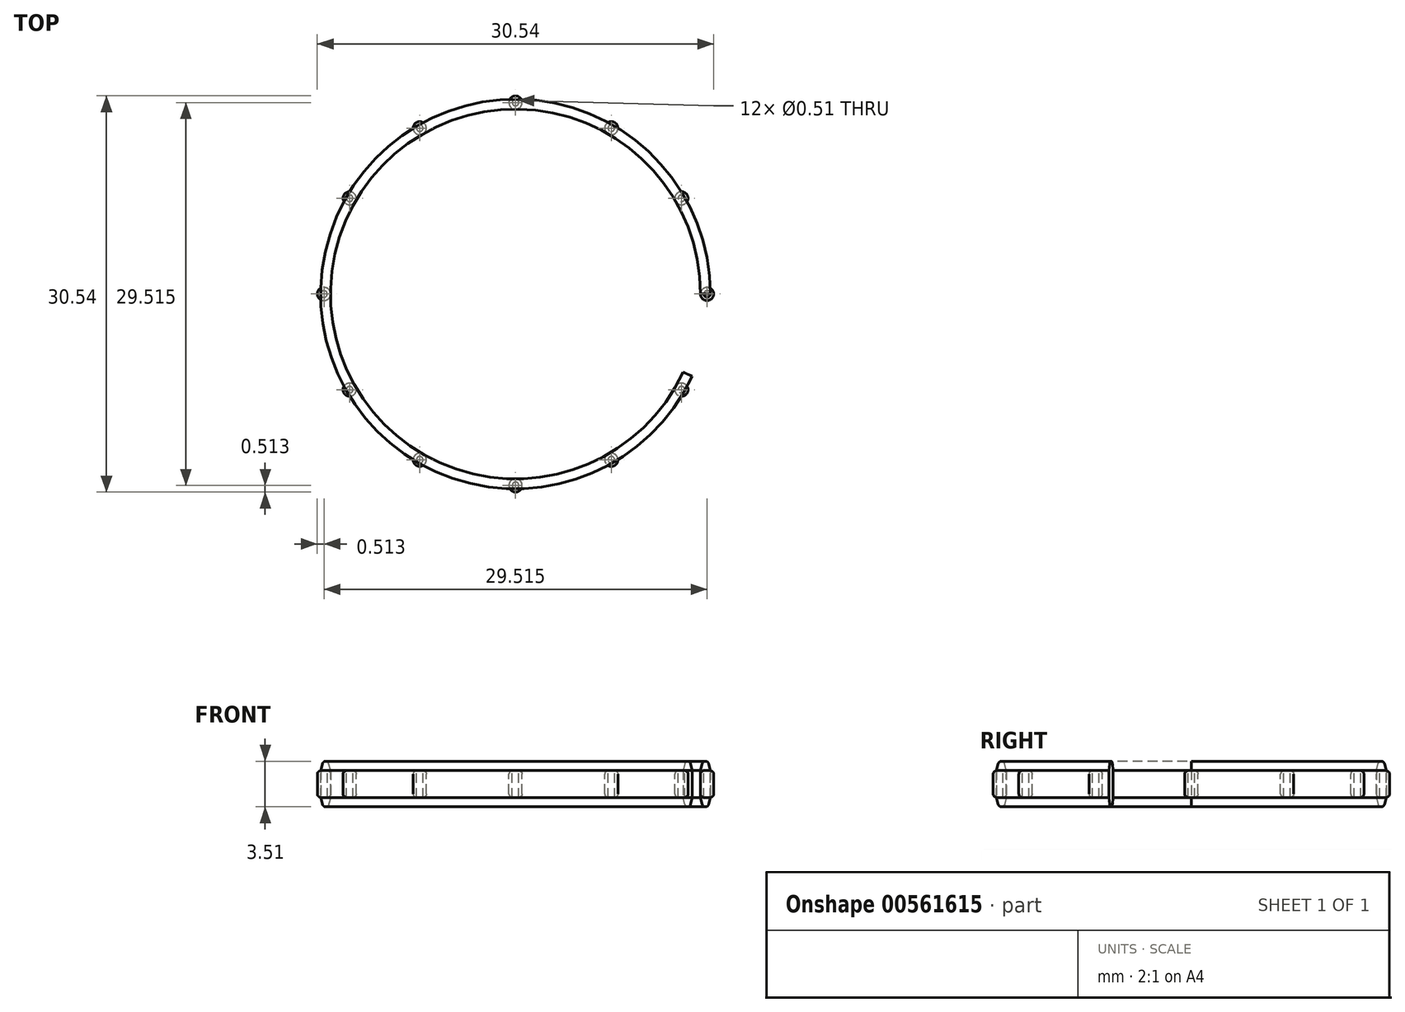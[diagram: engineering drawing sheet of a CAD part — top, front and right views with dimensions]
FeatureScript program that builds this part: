
annotation { "Feature Type Name" : "Feature", "Feature Type Description" : "" }
export const myFeature = defineFeature(function(context is Context, id is Id, definition is map)
    precondition{}
    {
        {
            var Q0;
            Q0=qCreatedBy(makeId("Front.planeOp"),FACE);
            var sketch = newSketch(context, id + "F0", { "sketchPlane" : qUnion([Q0])});
            skLineSegment(sketch, "E0", {"start": v(0, 0) * mm, "end": v(0, 3.94) * mm, "construction": true});
            skLineSegment(sketch, "E1", {"start": v(14.36, 2.54) * mm, "end": v(14.36, 0) * mm, "construction": true});
            skLineSegment(sketch, "E2", {"start": v(14.36, 0) * mm, "end": v(7.64, 0) * mm, "construction": true});
            skLineSegment(sketch, "E3", {"start": v(14.36, 2.54) * mm, "end": v(15.38, 2.54) * mm, "construction": true});
            skLineSegment(sketch, "E4", {"start": v(15.38, 2.54) * mm, "end": v(15.38, 0) * mm, "construction": true});
            skLineSegment(sketch, "E5", {"start": v(15.38, 0) * mm, "end": v(15.5, 0) * mm, "construction": true});
            skLineSegment(sketch, "E6", {"start": v(15.5, 0) * mm, "end": v(16, 0.5) * mm, "construction": true});
            skLineSegment(sketch, "E7", {"start": v(16, 0.5) * mm, "end": v(16, 4.02) * mm, "construction": true});
            skLineSegment(sketch, "E8", {"start": v(15.01, 1.85) * mm, "end": v(14.88, 2.35) * mm});
            skLineSegment(sketch, "E9", {"start": v(14.39, 2.35) * mm, "end": v(14.25, 1.85) * mm});
            skPoint(sketch, "E10.visualSharp", {"position": v(14.63, 3.27) * mm});
            skArc(sketch, "E10.filletArc", {"start": v(14.88, 2.35) * mm, "mid": v(14.63, 2.54) * mm, "end": v(14.39, 2.35) * mm});
            skArc(sketch, "E11.MirrorCS", {"start": v(14.88, -0.78) * mm, "mid": v(14.63, -0.97) * mm, "end": v(14.39, -0.78) * mm});
            skLineSegment(sketch, "E12.MirrorCS", {"start": v(15.01, -0.27) * mm, "end": v(14.88, -0.78) * mm});
            skLineSegment(sketch, "E13", {"start": v(13.69, -0.1) * mm, "end": v(16.72, -0.1) * mm, "construction": true});
            skLineSegment(sketch, "E14", {"start": v(13.24, -0.36) * mm, "end": v(17.66, -0.36) * mm, "construction": true});
            skLineSegment(sketch, "E15", {"start": v(13.22, -0.69) * mm, "end": v(17.76, -0.69) * mm, "construction": true});
            skLineSegment(sketch, "E16", {"start": v(14.63, 2.29) * mm, "end": v(14.63, -0.71) * mm, "construction": true});
            skLineSegment(sketch, "E17.trimOffspring", {"start": v(14.39, -0.78) * mm, "end": v(14.25, -0.27) * mm});
            skLineSegment(sketch, "E18", {"start": v(14.25, 1.85) * mm, "end": v(14.25, -0.27) * mm});
            skLineSegment(sketch, "E19", {"start": v(15.01, 1.85) * mm, "end": v(15.01, -0.27) * mm});
            skLineSegment(sketch, "E20.bottom", {"start": v(17.46, 3.65) * mm, "end": v(18.48, 3.65) * mm});
            skLineSegment(sketch, "E20.top", {"start": v(17.46, 1.01) * mm, "end": v(18.48, 1.01) * mm});
            skLineSegment(sketch, "E20.left", {"start": v(17.46, 3.65) * mm, "end": v(17.46, 1.01) * mm});
            skLineSegment(sketch, "E20.right", {"start": v(18.48, 3.65) * mm, "end": v(18.48, 1.01) * mm});
            skLineSegment(sketch, "E21", {"start": v(15.01, 1.85) * mm, "end": v(15.14, 1.77) * mm});
            skLineSegment(sketch, "E22", {"start": v(15.27, 1.55) * mm, "end": v(15.27, 0.02) * mm});
            skLineSegment(sketch, "E23", {"start": v(15.14, -0.2) * mm, "end": v(15.01, -0.27) * mm});
            skLineSegment(sketch, "E24", {"start": v(14.76, 2) * mm, "end": v(14.76, 0.25) * mm, "construction": true});
            skPoint(sketch, "E25.visualSharp", {"position": v(15.27, 1.7) * mm});
            skArc(sketch, "E25.filletArc", {"start": v(15.27, 1.55) * mm, "mid": v(15.23, 1.68) * mm, "end": v(15.14, 1.77) * mm});
            skPoint(sketch, "E26.visualSharp", {"position": v(15.27, -0.12) * mm});
            skArc(sketch, "E26.filletArc", {"start": v(15.14, -0.2) * mm, "mid": v(15.23, -0.1) * mm, "end": v(15.27, 0.02) * mm});
            skSolve(sketch);
        }
        {
            var Q0;
            Q0=makeQuery(id+"F0.imprint","IMPRINT",FACE,{"disambiguationData":[TD([[makeQuery(id+"F0.imprint","IMPRINT",EDGE,{"derivedFrom":sQuery(id+"F0.wireOp",EDGE,"E19")}),1.0]])]});
            var Q1;
            Q1=sQuery(id+"F0.wireOp",EDGE,"E24");
            revolve(context, id + "F1", {"entities" : qUnion([Q0]), "axis" : qUnion([Q1]), "revolveType" : RevolveType.FULL});
        }
        {
            var Q0;
            Q0=makeQuery(id+"F1.opRevolve","SWEPT_BODY",BODY,{"disambiguationData":[OSD([sQuery(id+"F0.wireOp",EDGE,"E19"),sQuery(id+"F0.wireOp",EDGE,"E21"),sQuery(id+"F0.wireOp",EDGE,"E22"),sQuery(id+"F0.wireOp",EDGE,"E23")])]});
            var Q1;
            Q1=sQuery(id+"F0.wireOp",EDGE,"E0");
            circularPattern(context, id + "F2", {"entities" : qUnion([Q0]), "axis" : qUnion([Q1]), "angle" : 360 * degree, "instanceCount" : 12, "equalSpace" : true});
        }
        {
            var Q0;
            Q0=makeQuery(id+"F0.imprint","IMPRINT",FACE,{"disambiguationData":[TD([[makeQuery(id+"F0.imprint","IMPRINT",EDGE,{"derivedFrom":sQuery(id+"F0.wireOp",EDGE,"E8")}),1.0]])]});
            var Q1;
            Q1=sQuery(id+"F0.wireOp",EDGE,"E0");
            revolve(context, id + "F3", {"entities" : qUnion([Q0]), "axis" : qUnion([Q1]), "revolveType" : RevolveType.ONE_DIRECTION, "angle" : 335 * degree});
        }
    });
